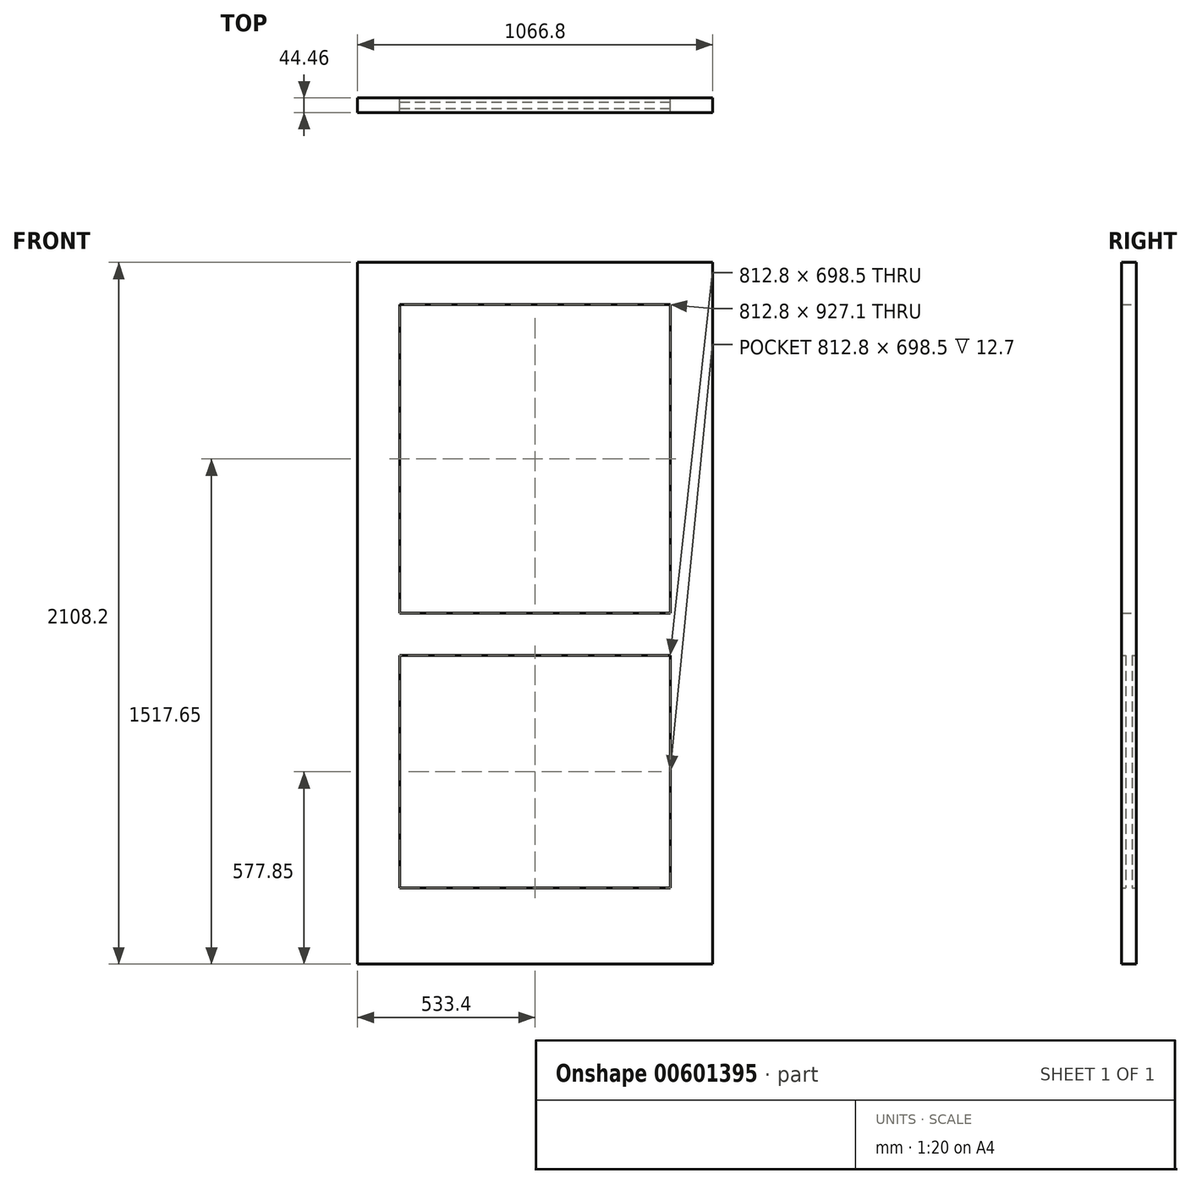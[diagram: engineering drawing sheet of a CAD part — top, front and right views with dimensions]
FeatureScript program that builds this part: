
annotation { "Feature Type Name" : "Feature", "Feature Type Description" : "" }
export const myFeature = defineFeature(function(context is Context, id is Id, definition is map)
    precondition{}
    {
        {
            var Q0;
            Q0=qCreatedBy(makeId("Front.planeOp"),FACE);
            var sketch = newSketch(context, id + "F0", { "sketchPlane" : qUnion([Q0])});
            skLineSegment(sketch, "E0.bottom", {"start": v(-533.4, 1054.1) * mm, "end": v(533.4, 1054.1) * mm});
            skLineSegment(sketch, "E0.top", {"start": v(-533.4, -1054.1) * mm, "end": v(533.4, -1054.1) * mm});
            skLineSegment(sketch, "E0.left", {"start": v(-533.4, 1054.1) * mm, "end": v(-533.4, -1054.1) * mm});
            skLineSegment(sketch, "E0.right", {"start": v(533.4, 1054.1) * mm, "end": v(533.4, -1054.1) * mm});
            skPoint(sketch, "E0.middle", {"position": v(0, 0) * mm});
            skLineSegment(sketch, "E1.bottom", {"start": v(-406.4, 927.1) * mm, "end": v(406.4, 927.1) * mm});
            skLineSegment(sketch, "E1.top", {"start": v(-406.4, -825.5) * mm, "end": v(406.4, -825.5) * mm});
            skLineSegment(sketch, "E1.left", {"start": v(-406.4, 927.1) * mm, "end": v(-406.4, -825.5) * mm});
            skLineSegment(sketch, "E1.right", {"start": v(406.4, 927.1) * mm, "end": v(406.4, -825.5) * mm});
            skPoint(sketch, "E1.middle", {"position": v(0, 50.8) * mm});
            skLineSegment(sketch, "E2.bottom", {"start": v(-406.4, 0) * mm, "end": v(406.4, 0) * mm});
            skLineSegment(sketch, "E2.top", {"start": v(-406.4, -127) * mm, "end": v(406.4, -127) * mm});
            skLineSegment(sketch, "E2.left", {"start": v(-406.4, 0) * mm, "end": v(-406.4, -127) * mm});
            skLineSegment(sketch, "E2.right", {"start": v(406.4, 0) * mm, "end": v(406.4, -127) * mm});
            skLineSegment(sketch, "E3.bottom", {"start": v(-38.1, 0) * mm, "end": v(38.1, 0) * mm});
            skLineSegment(sketch, "E3.top", {"start": v(-38.1, 927.1) * mm, "end": v(38.1, 927.1) * mm});
            skLineSegment(sketch, "E3.left", {"start": v(-38.1, 0) * mm, "end": v(-38.1, 927.1) * mm});
            skLineSegment(sketch, "E3.right", {"start": v(38.1, 0) * mm, "end": v(38.1, 927.1) * mm});
            skSolve(sketch);
        }
        {
            var Q0;
            Q0 = qSketchRegion(id + "F0", true);
            var Q1;
            Q1=makeQuery(id+"F0.imprint","IMPRINT",FACE,{"disambiguationData":[TD([[makeQuery(id+"F0.imprint","IMPRINT",EDGE,{"derivedFrom":sQuery(id+"F0.wireOp",EDGE,"E3.bottom")}),1.0]])]});
            var Q2;
            Q2=makeQuery(id+"F0.imprint","IMPRINT",FACE,{"disambiguationData":[TD([[makeQuery(id+"F0.imprint","IMPRINT",EDGE,{"derivedFrom":sQuery(id+"F0.wireOp",EDGE,"E2.top")}),1.0]])]});
            extrude(context, id + "F1", {"entities" : qUnion([Q0, Q1, Q2]), "endBound" : BoundingType.SYMMETRIC, "depth" : 44.45 * mm, "offsetDistance" : 25.4 * mm});
        }
        {
            var Q0;
            {var subQ0=sQuery(id+"F0.wireOp",EDGE,"E1.top");Q0=makeQuery(id+"F0.imprint","IMPRINT",FACE,{"disambiguationData":[TD([[makeQuery(id+"F0.imprint","IMPRINT",EDGE,{"derivedFrom":subQ0}),1.0]])]});}
            extrude(context, id + "F2", {"entities" : qUnion([Q0]), "operationType" : NewBodyOperationType.ADD, "endBound" : BoundingType.SYMMETRIC, "depth" : 19.05 * mm, "offsetDistance" : 25.4 * mm});
        }
    });
